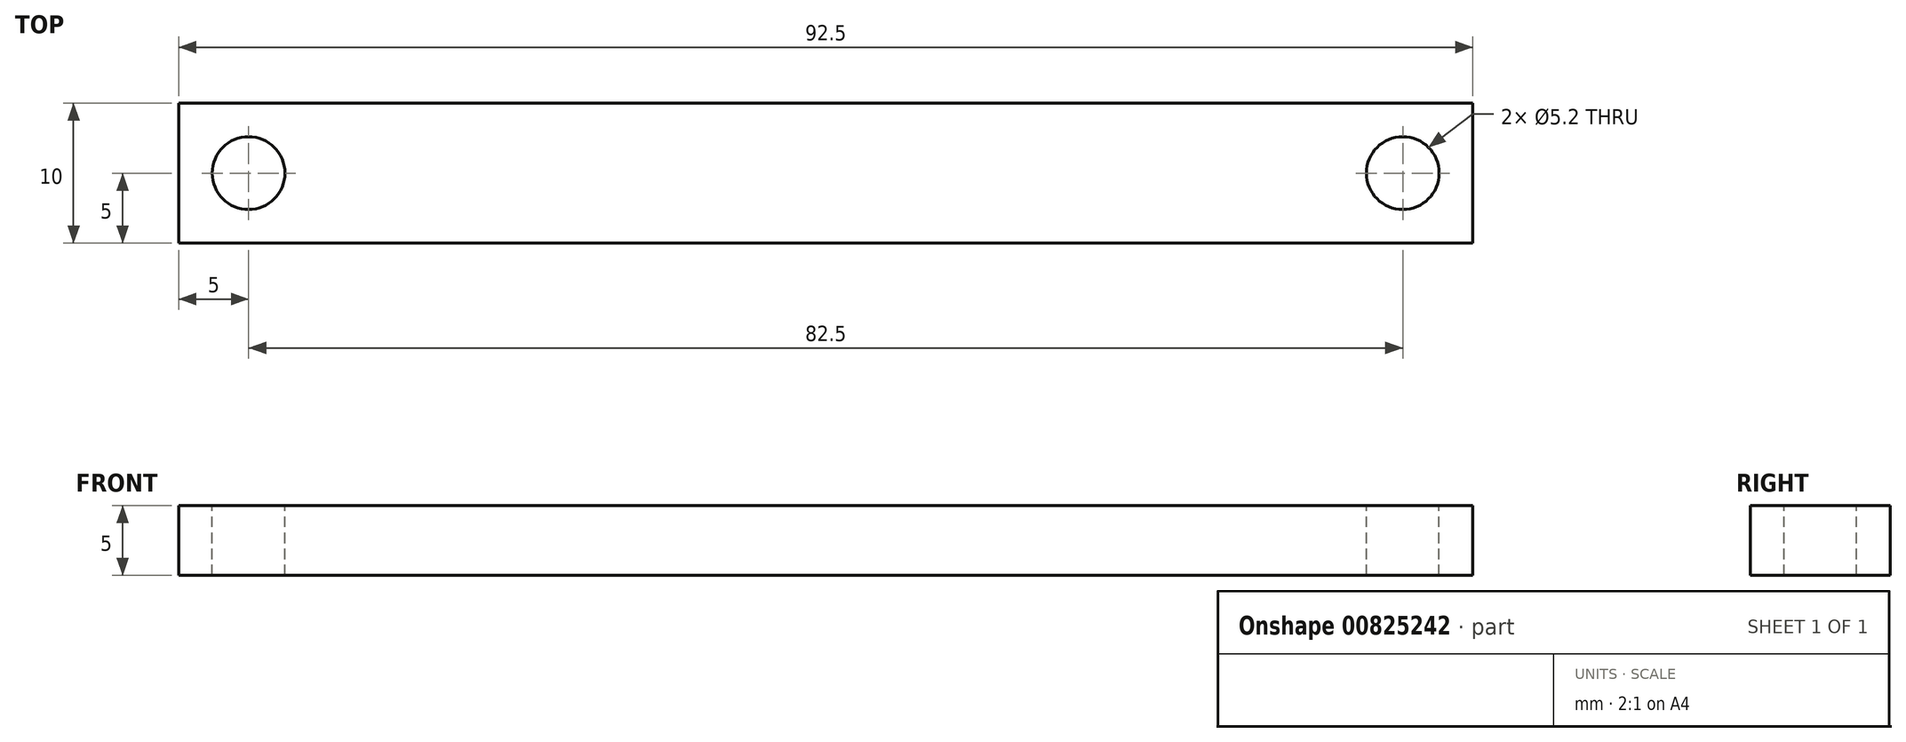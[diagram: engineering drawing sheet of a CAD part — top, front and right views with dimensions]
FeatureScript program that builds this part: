
annotation { "Feature Type Name" : "Feature", "Feature Type Description" : "" }
export const myFeature = defineFeature(function(context is Context, id is Id, definition is map)
    precondition{}
    {
        {
            var Q0;
            Q0=qCreatedBy(makeId("Top.planeOp"),FACE);
            var sketch = newSketch(context, id + "F0", { "sketchPlane" : qUnion([Q0])});
            skLineSegment(sketch, "E0.bottom", {"start": v(-46.25, -5) * mm, "end": v(46.25, -5) * mm});
            skLineSegment(sketch, "E0.top", {"start": v(-46.25, 5) * mm, "end": v(46.25, 5) * mm});
            skLineSegment(sketch, "E0.left", {"start": v(-46.25, -5) * mm, "end": v(-46.25, 5) * mm});
            skLineSegment(sketch, "E0.right", {"start": v(46.25, -5) * mm, "end": v(46.25, 5) * mm});
            skPoint(sketch, "E0.middle", {"position": v(0, 0) * mm});
            skSolve(sketch);
        }
        {
            var Q0;
            Q0 = qSketchRegion(id + "F0", true);
            extrude(context, id + "F1", {"entities" : qUnion([Q0]), "depth" : 5 * mm, "offsetDistance" : 25 * mm});
        }
        {
            var Q0;
            Q0=makeQuery(id+"F1.opExtrude","CAP_FACE",FACE,{"disambiguationData":[OSD([sQuery(id+"F0.wireOp",EDGE,"E0.bottom"),sQuery(id+"F0.wireOp",EDGE,"E0.top"),sQuery(id+"F0.wireOp",EDGE,"E0.left"),sQuery(id+"F0.wireOp",EDGE,"E0.right")])],"isStart":false});
            var sketch = newSketch(context, id + "F2", { "sketchPlane" : qUnion([Q0])});
            skLineSegment(sketch, "E1", {"start": v(-46.25, 0) * mm, "end": v(-41.25, 0) * mm});
            skCircle(sketch, "E2", {"center": v(-41.25, 0) * mm, "radius": 2.6 * mm});
            skSolve(sketch);
        }
        {
            var Q0;
            Q0 = qSketchRegion(id + "F2", true);
            extrude(context, id + "F3", {"entities" : qUnion([Q0]), "operationType" : NewBodyOperationType.REMOVE, "oppositeDirection" : true, "depth" : 25 * mm, "offsetDistance" : 25 * mm});
        }
        {
            var Q0;
            Q0=makeQuery(id+"F1.opExtrude","CAP_FACE",FACE,{"disambiguationData":[OSD([sQuery(id+"F0.wireOp",EDGE,"E0.bottom"),sQuery(id+"F0.wireOp",EDGE,"E0.top"),sQuery(id+"F0.wireOp",EDGE,"E0.left"),sQuery(id+"F0.wireOp",EDGE,"E0.right")])],"isStart":false});
            var sketch = newSketch(context, id + "F4", { "sketchPlane" : qUnion([Q0])});
            skLineSegment(sketch, "E3", {"start": v(46.25, 0) * mm, "end": v(41.25, 0) * mm});
            skCircle(sketch, "E4", {"center": v(41.25, 0) * mm, "radius": 2.6 * mm});
            skSolve(sketch);
        }
        {
            var Q0;
            Q0 = qSketchRegion(id + "F4", true);
            extrude(context, id + "F5", {"entities" : qUnion([Q0]), "operationType" : NewBodyOperationType.REMOVE, "oppositeDirection" : true, "depth" : 25 * mm, "offsetDistance" : 25 * mm});
        }
    });
